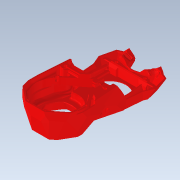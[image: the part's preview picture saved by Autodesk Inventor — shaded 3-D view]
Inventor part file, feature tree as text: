
AUTODESK INVENTOR PART (.ipt)
format: ipt  version: 2022.1 (Build 261234020, 234B)  size: 6,438,912 bytes
history: native  units: mm
features: delete_face x19, sketch x10, extrude x10, fillet x9, projected_geometry x8, chamfer x5, other x3, direct_edit x1, hole x1, reference x1, move_body x1
ambient origin geometry x8: Origin, YZ Plane, XZ Plane, XY Plane, X Axis, Y Axis, Z Axis, Center Point
bodies: Volumenkörper1 (feature_tree), Solid90 (feature_tree)
feature tree (68):
  sketch  "Skizze1"  dims[d0=0.1mm d1=0.1mm]
  extrude  "Extrusion1"  Depth=0.1mm
  delete_face  "Fläche löschen1"
  extrude  "Extrusion2"  Depth=0.1mm
  direct_edit  "Direktbearbeitung1"
  fillet  "Rundung1"  Radius=0.1mm
  extrude  "Extrusion3"  Depth=4.2mm TaperAngle=0.0deg
  chamfer  "Fase1"  Distance=2.0mm
  extrude  "Extrusion4"  Depth=0.3mm
  delete_face  "Fläche löschen2"
  delete_face  "Fläche löschen3"
  extrude  "Extrusion5"  Depth=0.4mm
  delete_face  "Fläche löschen4"
  fillet  "Rundung2"  Radius=0.4mm
  delete_face  "Fläche löschen5"
  delete_face  "Fläche löschen6"
  delete_face  "Fläche löschen7"
  sketch  "Skizze6"  dims[d16=0.6mm d17=0.4mm d18=0.4mm]
  extrude  "Extrusion6"  Depth=1.0mm TaperAngle=0.0deg
  extrude  "Extrusion7"  Depth=5.4mm
  delete_face  "Fläche löschen8"
  delete_face  "Fläche löschen9"
  extrude  "Extrusion8"  Depth=1.0mm TaperAngle=0.0deg
  delete_face  "Fläche löschen10"
  delete_face  "Fläche löschen11"
  delete_face  "Fläche löschen12"
  fillet  "Rundung3"  Radius=10.0mm
  delete_face  "Fläche löschen13"
  delete_face  "Fläche löschen14"
  extrude  "Extrusion9"  Depth=10.0mm TaperAngle=0.0deg
  chamfer  "Fase2"  Distance=10.0mm
  fillet  "Rundung4"  Radius=3.0mm
  fillet  "Rundung5"  Radius=1.0mm
  hole  "Bohrung1"  [1 undecoded]
  chamfer  "Fase3"  Distance=2.0mm Angle=45.0deg
  delete_face  "Fläche löschen15"
  extrude  "Extrusion10"  Depth=0.2mm
  delete_face  "Fläche löschen16"
  delete_face  "Fläche löschen17"
  delete_face  "Fläche löschen18"
  fillet  "Rundung6"  Radius=2.0mm
  fillet  "Rundung7"  Radius=0.4mm
  chamfer  "Fase4"  Distance=10.0mm
  chamfer  "Fase5"  Distance=2.0mm
  fillet  "Rundung8"  Radius=1.0mm
  fillet  "Rundung9"  Radius=0.4mm
  delete_face  "Fläche löschen19"
  reference  "Referenz1"
  sketch  "Skizze2"  dims[d3=0.1mm d4=0.1mm d5=0.1mm]
  projected_geometry  "Projizierte Kontur1"
  sketch  "Skizze3"  dims[d6=0.1mm d7=4.2mm d8=0.0mm]
  sketch  "Skizze4"  dims[d9=90.0deg d10=2.0mm d11=0.0mm]
  sketch  "Skizze5"  dims[d12=0.0mm d13=0.0mm d14=-0.5mm d15=0.3mm]
  projected_geometry  "Projizierte Kontur2"
  projected_geometry  "Projizierte Kontur3"
  projected_geometry  "Projizierte Kontur4"
  projected_geometry  "Projizierte Kontur5"
  sketch  "Skizze7"  dims[d19=0.4mm d20=1.0mm d21=0.0mm]
  projected_geometry  "Projizierte Kontur6"
  sketch  "Skizze8"  dims[d22=1.0mm d23=2.0mm d24=45.0deg d25=5.4mm]
  projected_geometry  "Projizierte Kontur7"
  sketch  "Skizze9"  dims[d26=5.4mm d27=1.0mm d28=0.0mm d29=10.0mm d30=0.0mm]
  sketch  "Skizze10"  dims[d31=2.0mm d32=10.0mm d33=0.0mm d34=10.0mm d35=0.0mm d36=3.0mm d37=0.0mm d38=1.0mm d39=3.0mm d40=0.0mm d41=0.32mm d42=2.0mm d43=45.0deg d44=1.4mm d45=2.0mm d46=2.95mm d47=6.0mm d48=5.7mm d49=3.4mm d50=90.0deg d51=3.8mm d52=90.0deg d53=0.4mm d54=2.0mm d55=45.0deg d56=10.0mm d57=0.0mm d58=2.0mm d59=1.0mm d60=0.4mm d61=2.0mm d62=45.0deg d63=0.4mm d64=2.0mm d65=45.0deg d66=0.4mm d67=2.4mm d68=0.2mm]
  projected_geometry  "Projizierte Kontur8"
  other  "<userpath>\Desktop\RAMA_SBNG\LGX_Lite_Stealthburner_zusammen.iam"
  other  "LGX_Lite_Stealthburner_zusammen.iam"
  other  "SB-FAN-PCB33:1"
  move_body  "Verschieben1"
note: 1 required parameter value undecoded (feature->parameter linkage not recoverable at this tier; creation-order binding heuristic only, values carry confidence <= 0.55)
